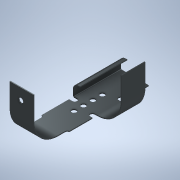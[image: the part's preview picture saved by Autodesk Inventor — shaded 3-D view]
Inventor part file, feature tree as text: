
AUTODESK INVENTOR PART (.ipt)
format: ipt  version: 2021 (Build 250183000, 183)  size: 241,152 bytes
history: native  units: in
note: dims shown in document units (in); Inventor stores cm internally (conversion verified against a paired STEP export)
features: sheet_metal_op x13, sketch x6, other x4, hole x2, pattern_linear x1
ambient origin geometry x8: Origin, YZ Plane, XZ Plane, XY Plane, X Axis, Y Axis, Z Axis, Center Point
bodies: Solid1 (feature_tree), Solid2 (feature_tree)
feature tree (26):
  sheet_metal_op  "Face1"
  sheet_metal_op  "Flange1"
  sheet_metal_op  "Flange2"
  sheet_metal_op  "Contour Flange1"
  sheet_metal_op  "Bend4"
  hole  "Hole1"  [1 undecoded]
  pattern_linear  "Rectangular Pattern1"  Spacing1=0.1in  [1 undecoded]
  hole  "Hole2"  [1 undecoded]
  sheet_metal_op  "Unfold1"
  sheet_metal_op  "Refold1"
  sketch  "Sketch1"  dims[d0=0.0197in d1=0.1in d2=0.2in d3=0.1in d4=0.0197in]
  other  "Plate1"
  sketch  "Sketch2"  dims[d5=1.0in d6=90.0deg d7=0.5in]
  other  "Plate2"
  sheet_metal_op  "Bend1"
  sheet_metal_op  "Corner1"
  sketch  "Sketch4"  dims[d8=0.5in]
  other  "Plate3"
  sheet_metal_op  "Bend2"
  sheet_metal_op  "Corner2"
  sketch  "Sketch5"  dims[d9=0.0787in]
  other  "Plate4"
  sheet_metal_op  "Bend3"
  sheet_metal_op  "Corner3"
  sketch  "Sketch6"  dims[d10=0.0197in]
  sketch  "Sketch7"  dims[d11=0.0197in d12=0.1in d13=0.1in d14=0.1in d15=0.0197in d16=0.5in d17=1.0in d18=90.0deg d19=0.5in d20=0.0787in d21=0.0197in d22=0.0197in d23=0.0197in d24=0.0197in d25=0.0098in d26=0.0394in d27=0.0197in d28=1.0in d29=0.1in d30=0.02in d31=0.0787in d32=0.0197in d33=0.0197in d34=0.1in d35=0.1in d36=0.1in d37=0.0197in d38=0.0197in d39=0.1in d40=0.75in d41=0.375in d42=0.25in d43=0.5635in d44=0.12in d45=0.8108in d46=1.5748in d48=0.2in d49=0.2633in d50=0.2361in d51=0.1in d52=0.75in d53=0.375in d54=0.25in d55=0.5635in d56=0.12in d57=0.8108in]
note: 3 required parameter values undecoded (feature->parameter linkage not recoverable at this tier; creation-order binding heuristic only, values carry confidence <= 0.55)
